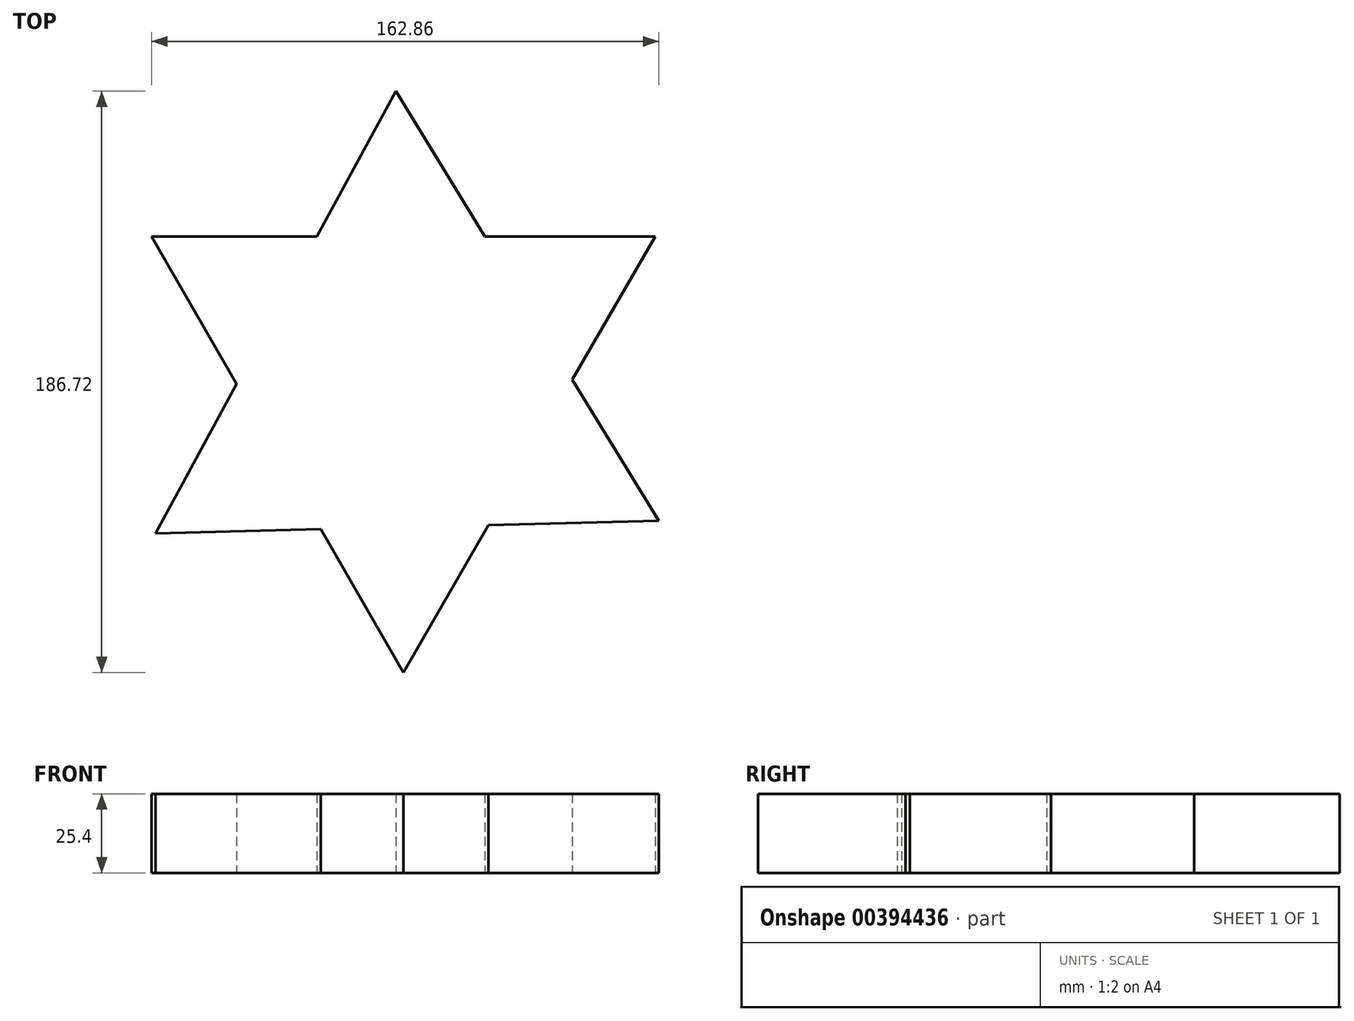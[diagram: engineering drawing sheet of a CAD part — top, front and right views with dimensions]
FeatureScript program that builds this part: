
annotation { "Feature Type Name" : "Feature", "Feature Type Description" : "" }
export const myFeature = defineFeature(function(context is Context, id is Id, definition is map)
    precondition{}
    {
        {
            var Q0;
            Q0=qCreatedBy(makeId("Top.planeOp"),FACE);
            var sketch = newSketch(context, id + "F0", { "sketchPlane" : qUnion([Q0])});
            skCircle(sketch, "E0.cCircle", {"center": v(0, 0) * mm, "radius": 46.69 * mm, "construction": true});
            skLineSegment(sketch, "E0.0", {"start": v(-2.33, 93.35) * mm, "end": v(82, -44.66) * mm});
            skLineSegment(sketch, "E0.1", {"start": v(82, -44.66) * mm, "end": v(-79.67, -48.7) * mm});
            skLineSegment(sketch, "E0.2", {"start": v(-79.67, -48.7) * mm, "end": v(-2.33, 93.35) * mm});
            skPoint(sketch, "E0.0.midPoint", {"position": v(39.84, 24.35) * mm});
            skLineSegment(sketch, "E1.0", {"start": v(-80.86, 46.69) * mm, "end": v(80.86, 46.69) * mm});
            skLineSegment(sketch, "E1.1", {"start": v(80.86, 46.69) * mm, "end": v(0, -93.37) * mm});
            skLineSegment(sketch, "E1.2", {"start": v(0, -93.37) * mm, "end": v(-80.86, 46.69) * mm});
            skPoint(sketch, "E1.0.midPoint", {"position": v(0, 46.69) * mm});
            skSolve(sketch);
        }
        {
            var Q0;
            {var subQ0=sQuery(id+"F0.wireOp",EDGE,"E1.2");var subQ1=sQuery(id+"F0.wireOp",EDGE,"E0.2");var subQ2=makeQuery(id+"F0.imprint","INTERSECT",VERTEX,{"derivedFrom":[subQ1,subQ0]});Q0=makeQuery(id+"F0.imprint","IMPRINT",FACE,{"disambiguationData":[TD([[makeQuery(id+"F0.imprint","IMPRINT",EDGE,{"disambiguationData":[TD([[subQ2,-1.0]])],"derivedFrom":subQ1}),1.0]])]});}
            var Q1;
            {var subQ0=sQuery(id+"F0.wireOp",EDGE,"E0.2");var subQ1=sQuery(id+"F0.wireOp",EDGE,"E0.0");var subQ2=makeQuery(id+"F0.imprint","INTERSECT",VERTEX,{"derivedFrom":[subQ1,subQ0]});Q1=makeQuery(id+"F0.imprint","IMPRINT",FACE,{"disambiguationData":[TD([[makeQuery(id+"F0.imprint","IMPRINT",EDGE,{"disambiguationData":[TD([[subQ2,-1.0]])],"derivedFrom":subQ1}),-1.0]])]});}
            var Q2;
            {var subQ0=sQuery(id+"F0.wireOp",EDGE,"E1.0");var subQ1=sQuery(id+"F0.wireOp",EDGE,"E0.0");var subQ2=makeQuery(id+"F0.imprint","INTERSECT",VERTEX,{"derivedFrom":[subQ1,subQ0]});Q2=makeQuery(id+"F0.imprint","IMPRINT",FACE,{"disambiguationData":[TD([[makeQuery(id+"F0.imprint","IMPRINT",EDGE,{"disambiguationData":[TD([[subQ2,-1.0]])],"derivedFrom":subQ1}),1.0]])]});}
            var Q3;
            {var subQ0=sQuery(id+"F0.wireOp",EDGE,"E0.1");var subQ1=sQuery(id+"F0.wireOp",EDGE,"E0.0");var subQ2=makeQuery(id+"F0.imprint","INTERSECT",VERTEX,{"derivedFrom":[subQ1,subQ0]});Q3=makeQuery(id+"F0.imprint","IMPRINT",FACE,{"disambiguationData":[TD([[makeQuery(id+"F0.imprint","IMPRINT",EDGE,{"disambiguationData":[TD([[subQ2,1.0]])],"derivedFrom":subQ1}),-1.0]])]});}
            var Q4;
            {var subQ0=sQuery(id+"F0.wireOp",EDGE,"E0.2");var subQ1=sQuery(id+"F0.wireOp",EDGE,"E0.1");var subQ2=makeQuery(id+"F0.imprint","INTERSECT",VERTEX,{"derivedFrom":[subQ1,subQ0]});Q4=makeQuery(id+"F0.imprint","IMPRINT",FACE,{"disambiguationData":[TD([[makeQuery(id+"F0.imprint","IMPRINT",EDGE,{"disambiguationData":[TD([[subQ2,1.0]])],"derivedFrom":subQ1}),-1.0]])]});}
            var Q5;
            {var subQ0=sQuery(id+"F0.wireOp",EDGE,"E1.1");var subQ1=sQuery(id+"F0.wireOp",EDGE,"E0.1");var subQ2=makeQuery(id+"F0.imprint","INTERSECT",VERTEX,{"derivedFrom":[subQ1,subQ0]});Q5=makeQuery(id+"F0.imprint","IMPRINT",FACE,{"disambiguationData":[TD([[makeQuery(id+"F0.imprint","IMPRINT",EDGE,{"disambiguationData":[TD([[subQ2,-1.0]])],"derivedFrom":subQ1}),1.0]])]});}
            var Q6;
            {var subQ0=sQuery(id+"F0.wireOp",EDGE,"E1.0");var subQ1=sQuery(id+"F0.wireOp",EDGE,"E0.0");var subQ2=makeQuery(id+"F0.imprint","INTERSECT",VERTEX,{"derivedFrom":[subQ1,subQ0]});Q6=makeQuery(id+"F0.imprint","IMPRINT",FACE,{"disambiguationData":[TD([[makeQuery(id+"F0.imprint","IMPRINT",EDGE,{"disambiguationData":[TD([[subQ2,-1.0]])],"derivedFrom":subQ1}),-1.0]])]});}
            extrude(context, id + "F1", {"entities" : qUnion([Q0, Q1, Q2, Q3, Q4, Q5, Q6]), "depth" : 25.4 * mm});
        }
    });
